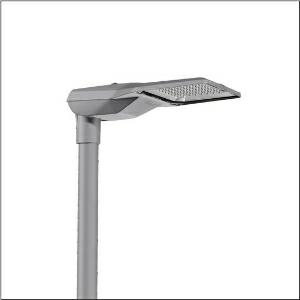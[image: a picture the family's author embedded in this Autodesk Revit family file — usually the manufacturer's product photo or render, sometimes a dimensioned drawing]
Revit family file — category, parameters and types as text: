
# Revit family: streetlight_sl_21_midi___p0_8ab_5xe3r33s08lb_9dc6
name_source: partatom
category: Lighting Fixtures
units: mm (PartAtom-declared; Revit-internal decimal feet)

## family parameters
Cut with Voids When Loaded = No
Host = Face
Light Source = No
Part Type = Normal
Room Calculation Point = No
Round Connector Dimension = Use Diameter
Shared = No

## types (1)
- --- (1 x LED, 12450 lm, 99.6 W, 3000K)
    Apparent Load = 100 VA
    CIE Flux Codes = 36 71 98 100 100
    Color Rendering = 70
    Color Temperature = 3000K
    Default Elevation = 1800 mm
    Description = Streetlight SL 21 midi, mast luminaire, primary light control with lens, of PMMA, primary optical cover: cover, of toughened safety glass, transparent, light distribution: P0.8aB, light emission: direct distribution, primary light characteristic: asymmetric, installation type: post-top, side-entry, LED, High Power LED, rated luminous flux: 12.450lm, luminous efficacy: 125lm/W, light colour: 730, colour temperature: 3000K, control gear: D4i, control: pre-setting: logarithmic dimming characteristic, flexible luminous flux parameterisation, time-dependent luminous flux control, constant luminous flux control, overheat protection, mains connection: 230..240V, AC, 50/60Hz, start of lifetime: 100W, end of service life: 102W, reduction: 46W, luminaire housing, of diecast aluminium, powder-coated, Siteco® metallic grey (DB 702S), corrosivity category C5 mid according to DIN EN ISO 12944, multi-level sealing system, sealing non-destructively replaceable, inclination adjustable: 0°, 5°, 10°, 15°, please order mast flange separately, length: 644mm, width: 335mm, height: 110mm, mast flange for spigot size: 42mm (side-entry): 5XC10008XM4, 60/48mm (side-entry/post-top): 5XC10108XM2, 76/60mm (side-entry/post-top): 5XC10108XM1, mounting height: 4..8m, Smart Interface above, protection rating (complete): IP66, insulation class (complete): insulation class II (safety insulation), certification: CE, ENEC, ENEC+, VDE, impact resistance: IK10, permissible operating ambient temperature for outdoor applications: -40..+50°C, standard-compliant lighting for roads and squares, packaging unit: 1 piece

Light Distribution: P0.8aB
    Height = 111 mm
    Lamp = 1 x LED
    Lamp Light Flux = 12450 lm
    Lamp Power = 99.6 W
    Lamp count = 1
    Length = 644 mm
    Luminous efficacy = 125 lm/W
    Manufacturer = Siteco
    ModVariant = No
    Model = 5XE3R33S08LB
    Number of Poles = 1
    OnlyDefault = Yes
    Power Factor = 1
    Product Name = Streetlight SL 21 midi | P0.8aB
    Product group = mast luminaire | pylon top
    ProductGroupID = 6100
    Protection Class = Protection class II
    Protection Degree = IP 66
    RLX_Detail_Level = 1
    RLX_Emergency_Light_Flux = 0 lm
    RLX_Emergency_Type = 0
    RLX_Emergency_Type_DB = No
    RlxData = <blob elided: 26409 chars, md5=f7a9d108>
    Socket = socket
    Standby Power = 0 W
    System Light Flux = 12450 lm
    System Power = 100 W
    Type Comments = factory setting: luminous flux: 100 % | dim-lin: 254 | 1020 mA
    Type Image = l_1004302.jpg
    URL = http://relux.com
    VarID = @adj_033547
    Voltage = 0 V
    Weight = 0.00 kg
    Width = 336 mm

## geometry (parser evidence)
native form markers: Blend x4, Sweep x12
no freeform markers — native parametric forms only
